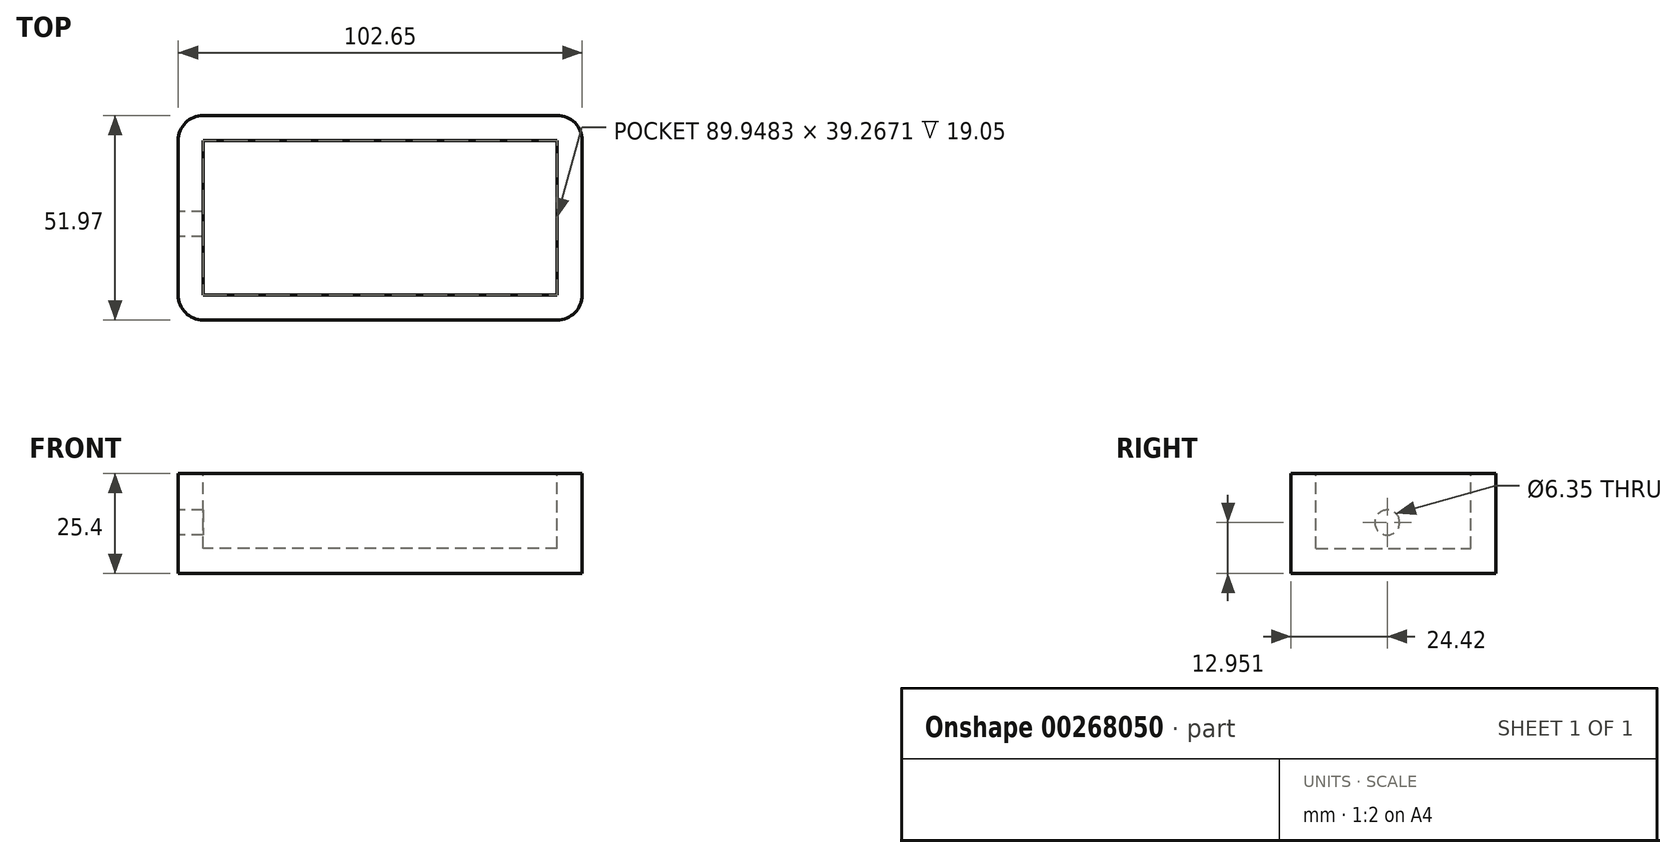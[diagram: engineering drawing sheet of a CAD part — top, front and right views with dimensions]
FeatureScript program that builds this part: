
annotation { "Feature Type Name" : "Feature", "Feature Type Description" : "" }
export const myFeature = defineFeature(function(context is Context, id is Id, definition is map)
    precondition{}
    {
        {
            var Q0;
            Q0=qCreatedBy(makeId("Top.planeOp"),FACE);
            var sketch = newSketch(context, id + "F0", { "sketchPlane" : qUnion([Q0])});
            skLineSegment(sketch, "E0.bottom", {"start": v(-48.8, -24.42) * mm, "end": v(53.86, -24.42) * mm});
            skLineSegment(sketch, "E0.top", {"start": v(-48.8, 27.55) * mm, "end": v(53.86, 27.55) * mm});
            skLineSegment(sketch, "E0.left", {"start": v(-48.8, -24.42) * mm, "end": v(-48.8, 27.55) * mm});
            skLineSegment(sketch, "E0.right", {"start": v(53.86, -24.42) * mm, "end": v(53.86, 27.55) * mm});
            skSolve(sketch);
        }
        {
            var Q0;
            Q0=makeQuery(id+"F0.imprint","IMPRINT",FACE,{"disambiguationData":[TD([[makeQuery(id+"F0.imprint","IMPRINT",EDGE,{"derivedFrom":sQuery(id+"F0.wireOp",EDGE,"E0.bottom")}),1.0]])]});
            extrude(context, id + "F1", {"entities" : qUnion([Q0]), "depth" : 25.4 * mm});
        }
        {
            var Q0;
            Q0=makeQuery(id+"F1.opExtrude","SWEPT_EDGE",EDGE,{"disambiguationData":[OSD([sQuery(id+"F0.wireOp",EDGE,"E0.bottom"),sQuery(id+"F0.wireOp",EDGE,"E0.left")])]});
            var Q1;
            Q1=makeQuery(id+"F1.opExtrude","SWEPT_EDGE",EDGE,{"disambiguationData":[OSD([sQuery(id+"F0.wireOp",EDGE,"E0.top"),sQuery(id+"F0.wireOp",EDGE,"E0.left")])]});
            var Q2;
            Q2=makeQuery(id+"F1.opExtrude","SWEPT_EDGE",EDGE,{"disambiguationData":[OSD([sQuery(id+"F0.wireOp",EDGE,"E0.bottom"),sQuery(id+"F0.wireOp",EDGE,"E0.right")])]});
            var Q3;
            Q3=makeQuery(id+"F1.opExtrude","SWEPT_EDGE",EDGE,{"disambiguationData":[OSD([sQuery(id+"F0.wireOp",EDGE,"E0.top"),sQuery(id+"F0.wireOp",EDGE,"E0.right")])]});
            fillet(context, id + "F2", {"entities" : qUnion([Q0, Q1, Q2, Q3]), "radius" : 6.35 * mm, "tangentPropagation" : true, "allowEdgeOverflow" : false});
        }
        {
            var Q0;
            Q0=makeQuery(id+"F1.opExtrude","CAP_FACE",FACE,{"disambiguationData":[OSD([sQuery(id+"F0.wireOp",EDGE,"E0.bottom"),sQuery(id+"F0.wireOp",EDGE,"E0.top"),sQuery(id+"F0.wireOp",EDGE,"E0.left"),sQuery(id+"F0.wireOp",EDGE,"E0.right")])],"isStart":false});
            var sketch = newSketch(context, id + "F3", { "sketchPlane" : qUnion([Q0])});
            skLineSegment(sketch, "E1.0", {"start": v(47.5, 21.2) * mm, "end": v(-42.44, 21.2) * mm});
            skLineSegment(sketch, "E1.1", {"start": v(47.5, -18.07) * mm, "end": v(47.5, 21.2) * mm});
            skLineSegment(sketch, "E1.2", {"start": v(-42.44, -18.07) * mm, "end": v(47.5, -18.07) * mm});
            skLineSegment(sketch, "E1.3", {"start": v(-42.44, 21.2) * mm, "end": v(-42.44, -18.07) * mm});
            skSolve(sketch);
        }
        {
            var Q0;
            Q0 = qSketchRegion(id + "F3", true);
            extrude(context, id + "F4", {"entities" : qUnion([Q0]), "operationType" : NewBodyOperationType.REMOVE, "oppositeDirection" : true, "depth" : 19.05 * mm});
        }
        {
            var Q0;
            Q0=makeQuery(id+"F1.opExtrude","SWEPT_FACE",FACE,{"disambiguationData":[OSD([sQuery(id+"F0.wireOp",EDGE,"E0.left")])]});
            var sketch = newSketch(context, id + "F5", { "sketchPlane" : qUnion([Q0])});
            skPoint(sketch, "E2", {"position": v(0, 12.95) * mm});
            skSolve(sketch);
        }
        {
            var Q0;
            Q0=sQuery(id+"F5.wireOp",VERTEX,"E2");
            var Q1;
            Q1=makeQuery(id+"F1.opExtrude","SWEPT_BODY",BODY,{"disambiguationData":[OSD([sQuery(id+"F0.wireOp",EDGE,"E0.bottom"),sQuery(id+"F0.wireOp",EDGE,"E0.top"),sQuery(id+"F0.wireOp",EDGE,"E0.left"),sQuery(id+"F0.wireOp",EDGE,"E0.right")])]});
            hole(context, id + "F6", {"style" : HoleStyle.SIMPLE, "endStyle" : HoleEndStyle.BLIND, "holeDiameter" : 6.35 * mm, "holeDepth" : 12.7 * mm, "tappedDepth" : 12.7 * mm, "tapClearance" : 3, "locations" : qUnion([Q0]), "scope" : qUnion([Q1])});
        }
    });
